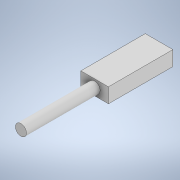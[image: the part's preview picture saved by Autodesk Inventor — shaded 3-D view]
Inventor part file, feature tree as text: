
AUTODESK INVENTOR PART (.ipt)
format: ipt  version: 2020 (Build 240168000, 168)  size: 104,448 bytes
history: native  units: mm
features: extrude x2, sketch x2
ambient origin geometry x8: Origin, YZ Plane, XZ Plane, XY Plane, X Axis, Y Axis, Z Axis, Center Point
bodies: Solid1 (feature_tree)
feature tree (4):
  extrude  "Extrusion1"  Depth=15.0mm
  extrude  "Extrusion2"  Depth=40.0mm
  sketch  "Sketch1"  dims[d0=35.0mm d1=15.0mm]
  sketch  "Sketch2"  dims[d2=8.0mm d3=0.0mm d4=7.5mm d5=4.0mm d6=6.0mm d7=40.0mm d8=0.0mm]
